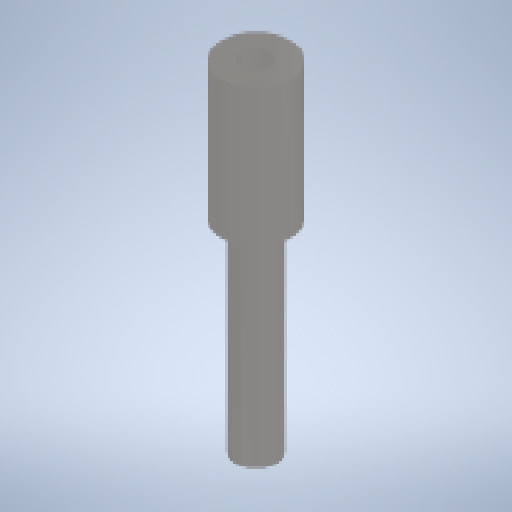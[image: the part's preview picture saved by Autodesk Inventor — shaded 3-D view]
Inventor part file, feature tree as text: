
AUTODESK INVENTOR PART (.ipt)
format: ipt  version: 2023 (Build 270158000, 158)  size: 147,968 bytes
history: native  units: mm
features: revolve x1, thread x1, sketch x1
ambient origin geometry x8: Origin, YZ Plane, XZ Plane, XY Plane, X Axis, Y Axis, Z Axis, Center Point
bodies: Solid1 (feature_tree)
feature tree (3):
  revolve  "Revolution1"  [1 undecoded]
  thread  "Thread1"  [1 undecoded]
  sketch  "Sketch1"  dims[d0=3.0mm d1=2.0mm d2=5.0mm d3=14.0mm d4=10.0mm d5=90.0deg d6=34.0mm d7=5.0mm d8=0.0mm]
note: 2 required parameter values undecoded (feature->parameter linkage not recoverable at this tier; creation-order binding heuristic only, values carry confidence <= 0.55)